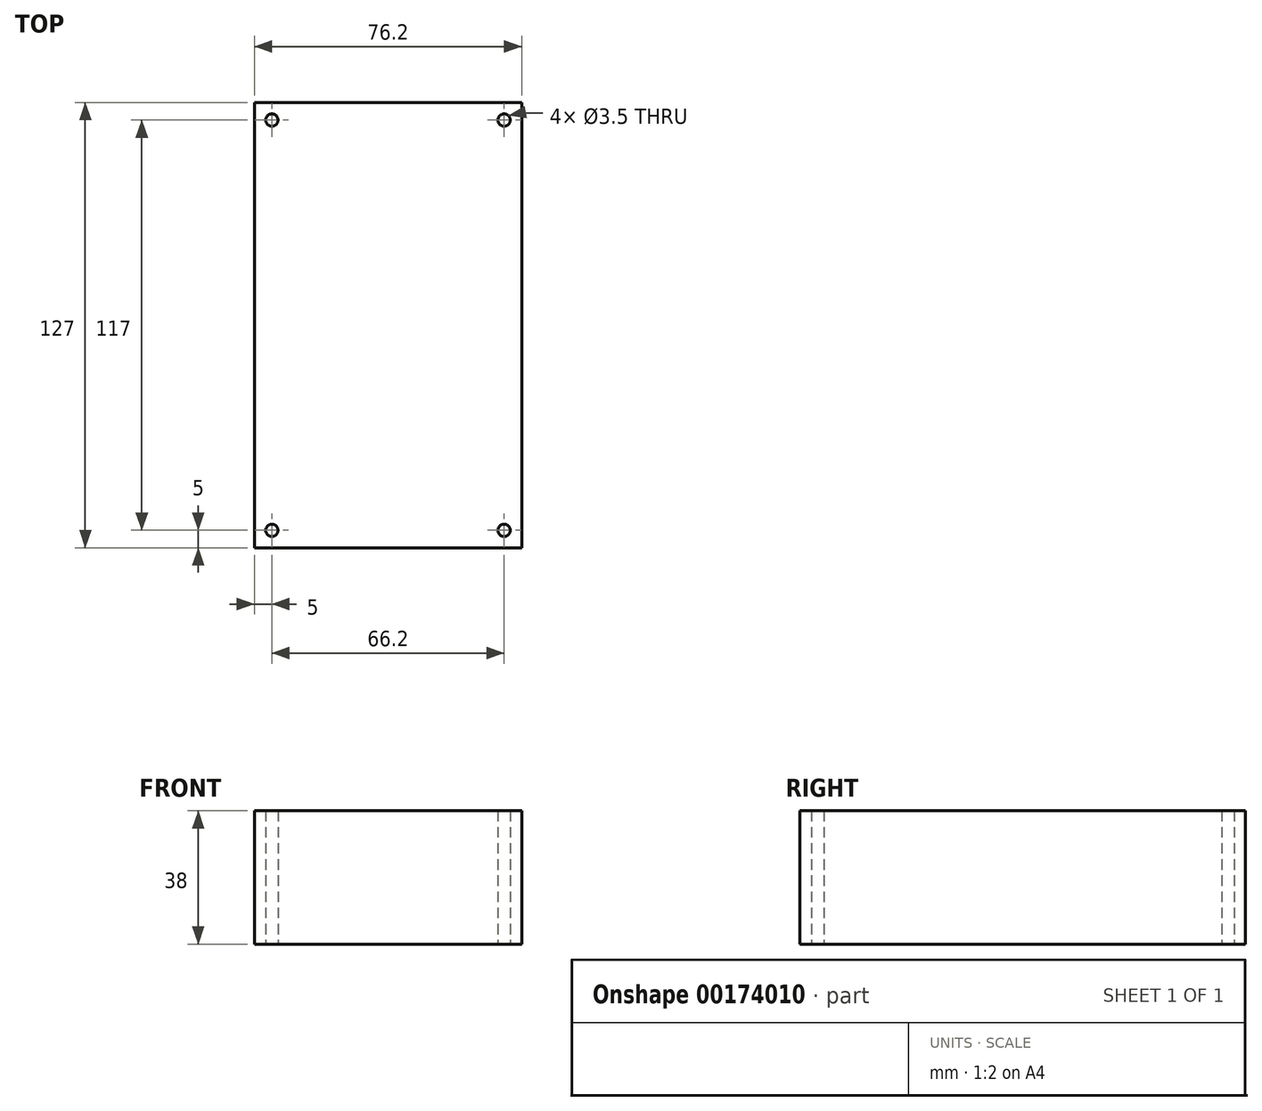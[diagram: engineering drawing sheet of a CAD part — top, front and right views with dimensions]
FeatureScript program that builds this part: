
annotation { "Feature Type Name" : "Feature", "Feature Type Description" : "" }
export const myFeature = defineFeature(function(context is Context, id is Id, definition is map)
    precondition{}
    {
        {
            var Q0;
            Q0=qCreatedBy(makeId("Top.planeOp"),FACE);
            var sketch = newSketch(context, id + "F0", { "sketchPlane" : qUnion([Q0])});
            skLineSegment(sketch, "E0.bottom", {"start": v(0, 0) * mm, "end": v(76.2, 0) * mm});
            skLineSegment(sketch, "E0.top", {"start": v(0, 127) * mm, "end": v(76.2, 127) * mm});
            skLineSegment(sketch, "E0.left", {"start": v(0, 0) * mm, "end": v(0, 127) * mm});
            skLineSegment(sketch, "E0.right", {"start": v(76.2, 0) * mm, "end": v(76.2, 127) * mm});
            skLineSegment(sketch, "E1.bottom", {"start": v(71.2, 122) * mm, "end": v(5, 122) * mm, "construction": true});
            skLineSegment(sketch, "E1.top", {"start": v(71.2, 5) * mm, "end": v(5, 5) * mm, "construction": true});
            skLineSegment(sketch, "E1.left", {"start": v(71.2, 122) * mm, "end": v(71.2, 5) * mm, "construction": true});
            skLineSegment(sketch, "E1.right", {"start": v(5, 122) * mm, "end": v(5, 5) * mm, "construction": true});
            skPoint(sketch, "E1.middle", {"position": v(38.1, 63.5) * mm});
            skPoint(sketch, "E1.middle.positionSnap0", {"position": v(0, 63.5) * mm});
            skPoint(sketch, "E1.middle.positionSnap1", {"position": v(38.1, 127) * mm});
            skPoint(sketch, "E1.centerSnap0", {"position": v(0, 63.5) * mm});
            skPoint(sketch, "E1.centerSnap1", {"position": v(38.1, 127) * mm});
            skCircle(sketch, "E2", {"center": v(5, 122) * mm, "radius": 1.75 * mm});
            skCircle(sketch, "E3", {"center": v(71.2, 122) * mm, "radius": 1.75 * mm});
            skCircle(sketch, "E4", {"center": v(71.2, 5) * mm, "radius": 1.75 * mm});
            skCircle(sketch, "E5", {"center": v(5, 5) * mm, "radius": 1.75 * mm});
            skSolve(sketch);
        }
        {
            var Q0;
            Q0 = qSketchRegion(id + "F0", true);
            extrude(context, id + "F1", {"entities" : qUnion([Q0]), "depth" : (35 + 3) * mm});
        }
    });
